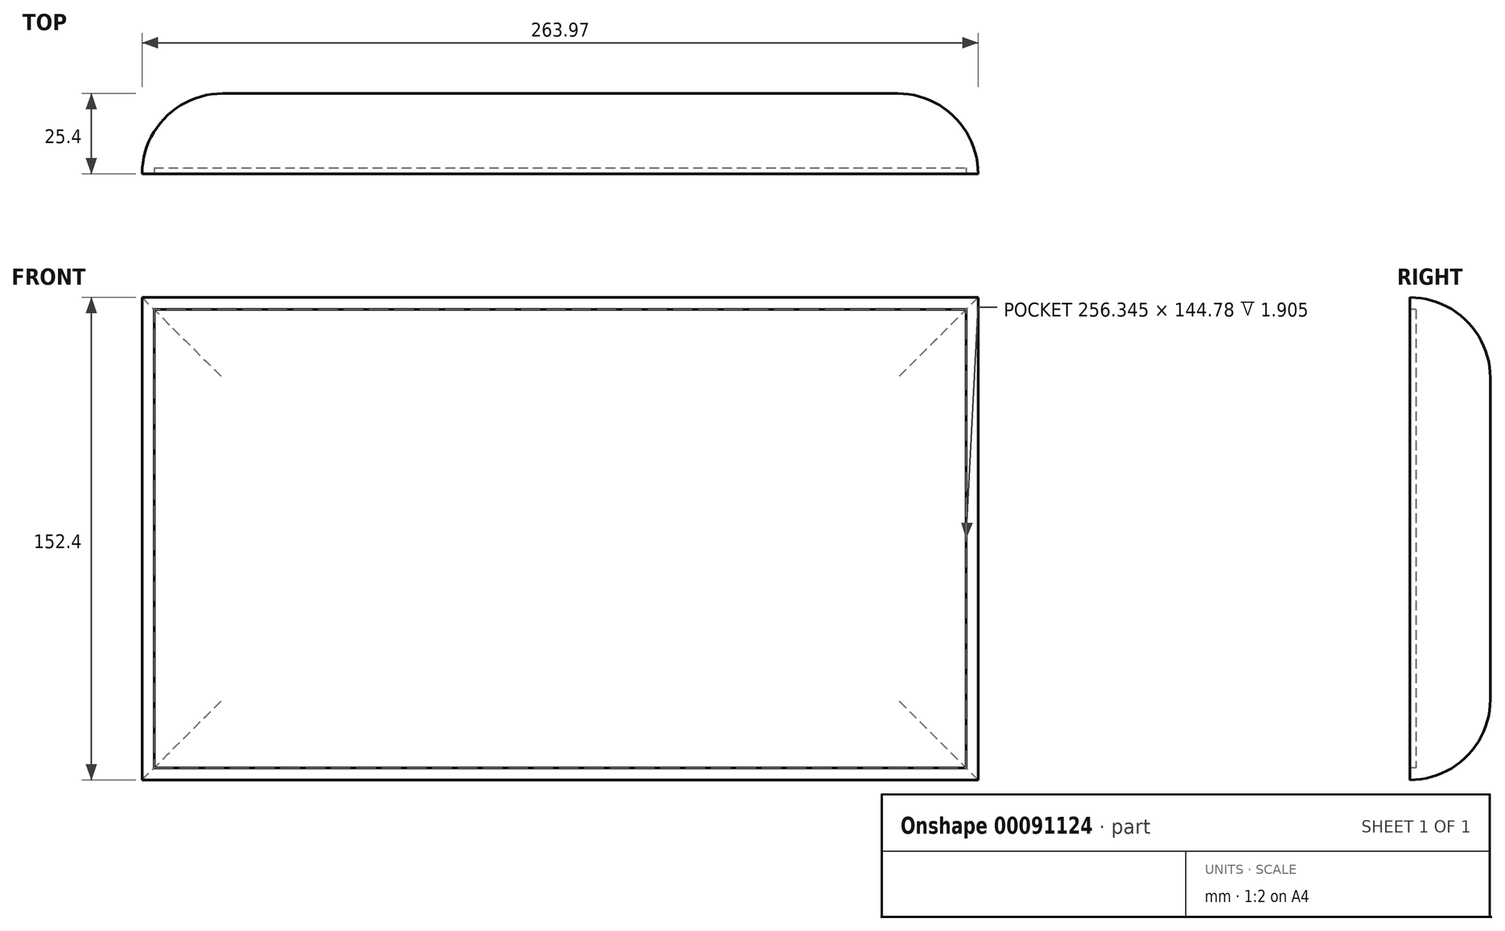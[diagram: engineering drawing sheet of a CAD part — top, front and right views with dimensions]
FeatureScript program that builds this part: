
annotation { "Feature Type Name" : "Feature", "Feature Type Description" : "" }
export const myFeature = defineFeature(function(context is Context, id is Id, definition is map)
    precondition{}
    {
        {
            var Q0;
            Q0=qCreatedBy(makeId("Front.planeOp"),FACE);
            var sketch = newSketch(context, id + "F0", { "sketchPlane" : qUnion([Q0])});
            skLineSegment(sketch, "E0.bottom", {"start": v(-131.99, 60.19) * mm, "end": v(131.98, 60.19) * mm});
            skLineSegment(sketch, "E0.top", {"start": v(-131.99, -92.21) * mm, "end": v(131.98, -92.21) * mm});
            skLineSegment(sketch, "E0.left", {"start": v(-131.99, 60.19) * mm, "end": v(-131.99, -92.21) * mm});
            skLineSegment(sketch, "E0.right", {"start": v(131.98, 60.19) * mm, "end": v(131.98, -92.21) * mm});
            skSolve(sketch);
        }
        {
            var Q0;
            Q0=makeQuery(id+"F0.imprint","IMPRINT",FACE,{"disambiguationData":[TD([[makeQuery(id+"F0.imprint","IMPRINT",EDGE,{"derivedFrom":sQuery(id+"F0.wireOp",EDGE,"E0.bottom")}),-1.0]])]});
            extrude(context, id + "F1", {"entities" : qUnion([Q0]), "depth" : 25.4 * mm});
        }
        {
            var Q0;
            Q0=makeQuery(id+"F1.opExtrude","CAP_FACE",FACE,{"disambiguationData":[OSD([sQuery(id+"F0.wireOp",EDGE,"E0.bottom"),sQuery(id+"F0.wireOp",EDGE,"E0.top"),sQuery(id+"F0.wireOp",EDGE,"E0.left"),sQuery(id+"F0.wireOp",EDGE,"E0.right")])],"isStart":false});
            var sketch = newSketch(context, id + "F2", { "sketchPlane" : qUnion([Q0])});
            skLineSegment(sketch, "E1.bottom", {"start": v(-128.18, 56.38) * mm, "end": v(128.17, 56.38) * mm});
            skLineSegment(sketch, "E1.top", {"start": v(-128.18, -88.4) * mm, "end": v(128.17, -88.4) * mm});
            skLineSegment(sketch, "E1.left", {"start": v(-128.18, 56.38) * mm, "end": v(-128.18, -88.4) * mm});
            skLineSegment(sketch, "E1.right", {"start": v(128.17, 56.38) * mm, "end": v(128.17, -88.4) * mm});
            skSolve(sketch);
        }
        {
            var Q0;
            Q0 = qSketchRegion(id + "F2", true);
            extrude(context, id + "F3", {"entities" : qUnion([Q0]), "operationType" : NewBodyOperationType.REMOVE, "oppositeDirection" : true, "depth" : 1.9 * mm});
        }
        {
            var Q0;
            Q0=makeQuery(id+"F1.opExtrude","CAP_EDGE",EDGE,{"disambiguationData":[OSD([sQuery(id+"F0.wireOp",EDGE,"E0.top")])],"isStart":true});
            var Q1;
            Q1=makeQuery(id+"F1.opExtrude","CAP_EDGE",EDGE,{"disambiguationData":[OSD([sQuery(id+"F0.wireOp",EDGE,"E0.right")])],"isStart":true});
            var Q2;
            Q2=makeQuery(id+"F1.opExtrude","CAP_EDGE",EDGE,{"disambiguationData":[OSD([sQuery(id+"F0.wireOp",EDGE,"E0.bottom")])],"isStart":true});
            var Q3;
            Q3=makeQuery(id+"F1.opExtrude","CAP_EDGE",EDGE,{"disambiguationData":[OSD([sQuery(id+"F0.wireOp",EDGE,"E0.left")])],"isStart":true});
            fillet(context, id + "F4", {"entities" : qUnion([Q0, Q1, Q2, Q3]), "radius" : 25.4 * mm, "tangentPropagation" : true, "allowEdgeOverflow" : false});
        }
    });
